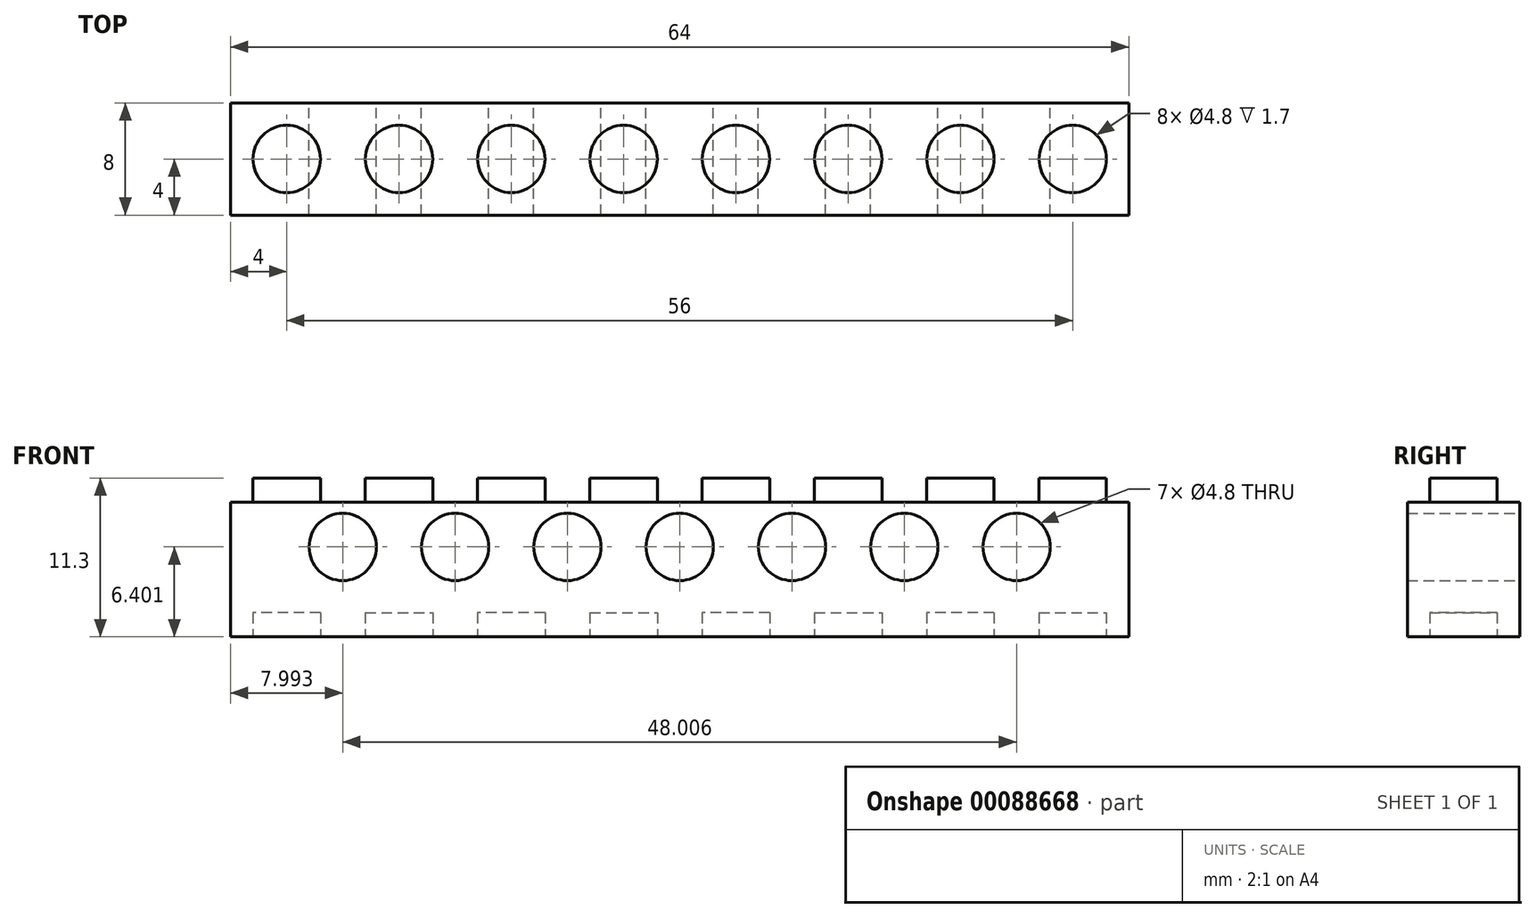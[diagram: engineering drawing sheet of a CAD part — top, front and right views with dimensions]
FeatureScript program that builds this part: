
annotation { "Feature Type Name" : "Feature", "Feature Type Description" : "" }
export const myFeature = defineFeature(function(context is Context, id is Id, definition is map)
    precondition{}
    {
        {
            var Q0;
            Q0=qCreatedBy(makeId("Front.planeOp"),FACE);
            var sketch = newSketch(context, id + "F0", { "sketchPlane" : qUnion([Q0])});
            skLineSegment(sketch, "E0.bottom", {"start": v(-4, 9.6) * mm, "end": v(-2.4, 9.6) * mm});
            skLineSegment(sketch, "E0.top", {"start": v(-4, 0) * mm, "end": v(4, 0) * mm});
            skLineSegment(sketch, "E0.left", {"start": v(-4, 9.6) * mm, "end": v(-4, 0) * mm});
            skLineSegment(sketch, "E0.right", {"start": v(4, 9.6) * mm, "end": v(4, 0) * mm});
            skLineSegment(sketch, "E1.top", {"start": v(-2.4, 11.3) * mm, "end": v(2.4, 11.3) * mm});
            skLineSegment(sketch, "E1.left", {"start": v(-2.4, 9.6) * mm, "end": v(-2.4, 11.3) * mm});
            skLineSegment(sketch, "E1.right", {"start": v(2.4, 9.6) * mm, "end": v(2.4, 11.3) * mm});
            skLineSegment(sketch, "E2", {"start": v(0, 0) * mm, "end": v(0, 24.04) * mm, "construction": true});
            skLineSegment(sketch, "E3.trimOffspring", {"start": v(2.4, 9.6) * mm, "end": v(4, 9.6) * mm});
            skSolve(sketch);
        }
        {
            var Q0;
            Q0=makeQuery(id+"F0.imprint","IMPRINT",FACE,{"disambiguationData":[TD([[makeQuery(id+"F0.imprint","IMPRINT",EDGE,{"derivedFrom":sQuery(id+"F0.wireOp",EDGE,"E0.bottom")}),-1.0]])]});
            extrude(context, id + "F1", {"entities" : qUnion([Q0]), "depth" : 8 * mm});
        }
        {
            var Q0;
            Q0=qCreatedBy(makeId("Top.planeOp"),FACE);
            var Q1;
            Q1=makeQuery(id+"F1.opExtrude","CAP_VERTEX",VERTEX,{"disambiguationData":[OSD([sQuery(id+"F0.wireOp",EDGE,"E1.top"),sQuery(id+"F0.wireOp",EDGE,"E1.right")])],"isStart":true});
            cPlane(context, id + "F2", {"entities" : qUnion([Q0, Q1]), "cplaneType" : CPlaneType.PLANE_POINT, "offset" : 152.4 * mm, "width" : 152.4 * mm, "height" : 152.4 * mm});
        }
        {
            var Q0;
            Q0=qCreatedBy(id+"F2.planeOp",FACE);
            var sketch = newSketch(context, id + "F3", { "sketchPlane" : qUnion([Q0])});
            skLineSegment(sketch, "E4.0", {"start": v(-4, -8) * mm, "end": v(-4, 0) * mm});
            skLineSegment(sketch, "E5.0", {"start": v(4, -8) * mm, "end": v(4, 0) * mm});
            skLineSegment(sketch, "E6", {"start": v(-4, 0) * mm, "end": v(4, 0) * mm});
            skLineSegment(sketch, "E7", {"start": v(-4, -8) * mm, "end": v(4, -8) * mm});
            skLineSegment(sketch, "E8", {"start": v(-4, 0) * mm, "end": v(4, -8) * mm, "construction": true});
            skLineSegment(sketch, "E9", {"start": v(-4, -8) * mm, "end": v(4, 0) * mm, "construction": true});
            skCircle(sketch, "E10", {"center": v(0, -4) * mm, "radius": 2.4 * mm});
            skSolve(sketch);
        }
        {
            var Q0;
            Q0=qSketchRegion(id+"F3",true);
            var Q1;
            Q1=makeQuery(id+"F1.opExtrude","SWEPT_FACE",FACE,{"disambiguationData":[OSD([sQuery(id+"F0.wireOp",EDGE,"E0.bottom")])]});
            extrude(context, id + "F4", {"entities" : qUnion([Q0]), "operationType" : NewBodyOperationType.REMOVE, "endBound" : BoundingType.UP_TO_SURFACE, "oppositeDirection" : true, "endBoundEntityFace" : qUnion([Q1]), "depth" : 25.4 * mm});
        }
        {
            var Q0;
            Q0=qCreatedBy(makeId("Top.planeOp"),FACE);
            var sketch = newSketch(context, id + "F5", { "sketchPlane" : qUnion([Q0])});
            skCircle(sketch, "E11.0", {"center": v(0, -4) * mm, "radius": 2.4 * mm});
            skSolve(sketch);
        }
        {
            var Q0;
            Q0=makeQuery(id+"F5.imprint","IMPRINT",FACE,{"disambiguationData":[TD([[makeQuery(id+"F5.imprint","IMPRINT",EDGE,{"derivedFrom":sQuery(id+"F5.wireOp",EDGE,"E11.0")}),1.0]])]});
            extrude(context, id + "F6", {"entities" : qUnion([Q0]), "operationType" : NewBodyOperationType.REMOVE, "depth" : 1.7 * mm});
        }
        {
            var Q0;
            Q0=qCreatedBy(makeId("Right.planeOp"),FACE);
            var Q1;
            Q1=makeQuery(id+"F1.opExtrude","CAP_VERTEX",VERTEX,{"disambiguationData":[OSD([sQuery(id+"F0.wireOp",EDGE,"E0.right"),sQuery(id+"F0.wireOp",EDGE,"E3.trimOffspring")])],"isStart":false});
            cPlane(context, id + "F7", {"entities" : qUnion([Q0, Q1]), "cplaneType" : CPlaneType.PLANE_POINT, "offset" : 152.4 * mm, "width" : 152.4 * mm, "height" : 152.4 * mm});
        }
        {
            var Q0;
            Q0=makeQuery(id+"F1.opExtrude","SWEPT_BODY",BODY,{"disambiguationData":[OSD([sQuery(id+"F0.wireOp",EDGE,"E0.bottom"),sQuery(id+"F0.wireOp",EDGE,"E0.top"),sQuery(id+"F0.wireOp",EDGE,"E0.left"),sQuery(id+"F0.wireOp",EDGE,"E0.right"),sQuery(id+"F0.wireOp",EDGE,"E1.top"),sQuery(id+"F0.wireOp",EDGE,"E1.left"),sQuery(id+"F0.wireOp",EDGE,"E1.right"),sQuery(id+"F0.wireOp",EDGE,"E3.trimOffspring")])]});
            var Q1;
            Q1=qCreatedBy(id+"F7.planeOp",FACE);
            mirror(context, id + "F8", {"operationType" : NewBodyOperationType.ADD, "entities" : qUnion([Q0]), "mirrorPlane" : qUnion([Q1])});
        }
        {
            var Q0;
            Q0=qCreatedBy(id+"F7.planeOp",FACE);
            var Q1;
            Q1=makeQuery(id+"F8.opPattern","COPY",VERTEX,{"derivedFrom":makeQuery(id+"F1.opExtrude","CAP_VERTEX",VERTEX,{"disambiguationData":[OSD([sQuery(id+"F0.wireOp",EDGE,"E0.bottom"),sQuery(id+"F0.wireOp",EDGE,"E0.left")])],"isStart":false}),"instanceName":"1"});
            cPlane(context, id + "F9", {"entities" : qUnion([Q0, Q1]), "cplaneType" : CPlaneType.PLANE_POINT, "offset" : 152.4 * mm, "width" : 152.4 * mm, "height" : 152.4 * mm});
        }
        {
            var Q0;
            Q0=makeQuery(id+"F1.opExtrude","SWEPT_BODY",BODY,{"disambiguationData":[OSD([sQuery(id+"F0.wireOp",EDGE,"E0.bottom"),sQuery(id+"F0.wireOp",EDGE,"E0.top"),sQuery(id+"F0.wireOp",EDGE,"E0.left"),sQuery(id+"F0.wireOp",EDGE,"E0.right"),sQuery(id+"F0.wireOp",EDGE,"E1.top"),sQuery(id+"F0.wireOp",EDGE,"E1.left"),sQuery(id+"F0.wireOp",EDGE,"E1.right"),sQuery(id+"F0.wireOp",EDGE,"E3.trimOffspring")])]});
            var Q1;
            Q1=qCreatedBy(id+"F9.planeOp",FACE);
            mirror(context, id + "F10", {"operationType" : NewBodyOperationType.ADD, "entities" : qUnion([Q0]), "mirrorPlane" : qUnion([Q1])});
        }
        {
            var Q0;
            Q0=qCreatedBy(makeId("Right.planeOp"),FACE);
            var Q1;
            Q1=makeQuery(id+"F10.opPattern","COPY",VERTEX,{"derivedFrom":makeQuery(id+"F1.opExtrude","CAP_VERTEX",VERTEX,{"disambiguationData":[OSD([sQuery(id+"F0.wireOp",EDGE,"E0.bottom"),sQuery(id+"F0.wireOp",EDGE,"E0.left")])],"isStart":false}),"instanceName":"1"});
            cPlane(context, id + "F11", {"entities" : qUnion([Q0, Q1]), "cplaneType" : CPlaneType.PLANE_POINT, "offset" : 152.4 * mm, "width" : 152.4 * mm, "height" : 152.4 * mm});
        }
        {
            var Q0;
            Q0=makeQuery(id+"F1.opExtrude","SWEPT_BODY",BODY,{"disambiguationData":[OSD([sQuery(id+"F0.wireOp",EDGE,"E0.bottom"),sQuery(id+"F0.wireOp",EDGE,"E0.top"),sQuery(id+"F0.wireOp",EDGE,"E0.left"),sQuery(id+"F0.wireOp",EDGE,"E0.right"),sQuery(id+"F0.wireOp",EDGE,"E1.top"),sQuery(id+"F0.wireOp",EDGE,"E1.left"),sQuery(id+"F0.wireOp",EDGE,"E1.right"),sQuery(id+"F0.wireOp",EDGE,"E3.trimOffspring")])]});
            var Q1;
            Q1=qCreatedBy(id+"F11.planeOp",FACE);
            mirror(context, id + "F12", {"operationType" : NewBodyOperationType.ADD, "entities" : qUnion([Q0]), "mirrorPlane" : qUnion([Q1])});
        }
        {
            var Q0;
            Q0=qCreatedBy(makeId("Front.planeOp"),FACE);
            var sketch = newSketch(context, id + "F13", { "sketchPlane" : qUnion([Q0])});
            skLineSegment(sketch, "E12.0", {"start": v(47.65, 9.6) * mm, "end": v(60, 9.6) * mm, "construction": true});
            skLineSegment(sketch, "E13.0", {"start": v(60, 9.6) * mm, "end": v(60, 0) * mm, "construction": true});
            skLineSegment(sketch, "E14.0", {"start": v(47.65, 0) * mm, "end": v(60, 0) * mm, "construction": true});
            skLineSegment(sketch, "E15.0", {"start": v(47.65, 9.6) * mm, "end": v(47.65, 0) * mm, "construction": true});
            skCircle(sketch, "E16", {"center": v(52, 6.4) * mm, "radius": 2.4 * mm});
            skCircle(sketch, "E17", {"center": v(44, 6.4) * mm, "radius": 2.4 * mm});
            skCircle(sketch, "E18", {"center": v(36, 6.4) * mm, "radius": 2.4 * mm});
            skCircle(sketch, "E19.1.0.0", {"center": v(28, 6.4) * mm, "radius": 2.4 * mm});
            skCircle(sketch, "E19.2.0.0", {"center": v(20, 6.4) * mm, "radius": 2.4 * mm});
            skLineSegment(sketch, "E19.direction1", {"start": v(36, 6.4) * mm, "end": v(28, 6.4) * mm, "construction": true});
            skCircle(sketch, "E20.1.0.0", {"center": v(12, 6.4) * mm, "radius": 2.4 * mm});
            skCircle(sketch, "E20.2.0.0", {"center": v(4, 6.4) * mm, "radius": 2.4 * mm});
            skLineSegment(sketch, "E20.direction1", {"start": v(20, 6.4) * mm, "end": v(12, 6.4) * mm, "construction": true});
            skSolve(sketch);
        }
        {
            var Q0;
            Q0 = qSketchRegion(id + "F13", true);
            extrude(context, id + "F14", {"entities" : qUnion([Q0]), "operationType" : NewBodyOperationType.REMOVE, "depth" : 25.4 * mm});
        }
    });
